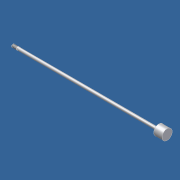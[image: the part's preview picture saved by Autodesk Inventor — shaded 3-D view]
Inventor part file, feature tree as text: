
AUTODESK INVENTOR PART (.ipt)
format: ipt  version: 2012 (Build 160160000, 160)  size: 136,704 bytes
history: native  units: in
note: dims shown in document units (in); Inventor stores cm internally (conversion verified against a paired STEP export)
features: other x112, sketch x3, revolve x2, thread x1, extrude x1
ambient origin geometry x8: Origin, YZ Plane, XZ Plane, XY Plane, X Axis, Y Axis, Z Axis, Center Point
bodies: Solid1 (feature_tree)
feature tree (119):
  revolve  "Revolution1"  Angle=360.0deg
  revolve  "Revolution2"  [1 undecoded]
  thread  "Thread1"  [1 undecoded]
  extrude  "Extrusion1"  [1 undecoded]
  other  "rod_cp_XY"
  other  "rod_cp_YZ"
  other  "rod_cp_ZX"
  other  "rod_cp_X"
  other  "rod_cp_Y"
  other  "rod_cp_Z"
  other  "rod_cp_Center"
  other  "to_rod_clevis_XY"
  other  "to_rod_clevis_YZ"
  other  "to_rod_clevis_ZX"
  other  "to_rod_clevis_X"
  other  "to_rod_clevis_Y"
  other  "to_rod_clevis_Z"
  other  "to_rod_clevis_Center"
  other  "rl2_XY"
  other  "rl2_YZ"
  other  "rl2_ZX"
  other  "rl2_X"
  other  "rl2_Y"
  other  "rl2_Z"
  other  "rl2_Center"
  other  "rl1_XY"
  other  "rl1_YZ"
  other  "rl1_ZX"
  other  "rl1_X"
  other  "rl1_Y"
  other  "rl1_Z"
  other  "rl1_Center"
  other  "thd1_XY"
  other  "thd1_YZ"
  other  "thd1_ZX"
  other  "thd1_X"
  other  "thd1_Y"
  other  "thd1_Z"
  other  "thd1_Center"
  other  "thd2_XY"
  other  "thd2_YZ"
  other  "thd2_ZX"
  other  "thd2_X"
  other  "thd2_Y"
  other  "thd2_Z"
  other  "thd2_Center"
  other  "dia1_XY"
  other  "dia1_YZ"
  other  "dia1_ZX"
  other  "dia1_X"
  other  "dia1_Y"
  other  "dia1_Z"
  other  "dia1_Center"
  other  "dia2_XY"
  other  "dia2_YZ"
  other  "dia2_ZX"
  other  "dia2_X"
  other  "dia2_Y"
  other  "dia2_Z"
  other  "dia2_Center"
  other  "wf1_XY"
  other  "wf1_YZ"
  other  "wf1_ZX"
  other  "wf1_X"
  other  "wf1_Y"
  other  "wf1_Z"
  other  "wf1_Center"
  other  "wf2_XY"
  other  "wf2_YZ"
  other  "wf2_ZX"
  other  "wf2_X"
  other  "wf2_Y"
  other  "wf2_Z"
  other  "wf2_Center"
  other  "hh1_XY"
  other  "hh1_YZ"
  other  "hh1_ZX"
  other  "hh1_X"
  other  "hh1_Y"
  other  "hh1_Z"
  other  "hh1_Center"
  other  "hh2_XY"
  other  "hh2_YZ"
  other  "hh2_ZX"
  other  "hh2_X"
  other  "hh2_Y"
  other  "hh2_Z"
  other  "hh2_Center"
  other  "dia12_XY"
  other  "dia12_YZ"
  other  "dia12_ZX"
  other  "dia12_X"
  other  "dia12_Y"
  other  "dia12_Z"
  other  "dia12_Center"
  other  "dia22_XY"
  other  "dia22_YZ"
  other  "dia22_ZX"
  other  "dia22_X"
  other  "dia22_Y"
  other  "dia22_Z"
  other  "dia22_Center"
  other  "wfw1_XY"
  other  "wfw1_YZ"
  other  "wfw1_ZX"
  other  "wfw1_X"
  other  "wfw1_Y"
  other  "wfw1_Z"
  other  "wfw1_Center"
  other  "wfw2_XY"
  other  "wfw2_YZ"
  other  "wfw2_ZX"
  other  "wfw2_X"
  other  "wfw2_Y"
  other  "wfw2_Z"
  other  "wfw2_Center"
  sketch  "Sketch_1"  dims[d0=360.0deg d1=360.0deg]
  sketch  "Sketch_3"  dims[d2=0.5in d3=0.0in d4=0.125in d5=0.0in]
  sketch  "Sketch_10"
note: 3 required parameter values undecoded (feature->parameter linkage not recoverable at this tier; creation-order binding heuristic only, values carry confidence <= 0.55)